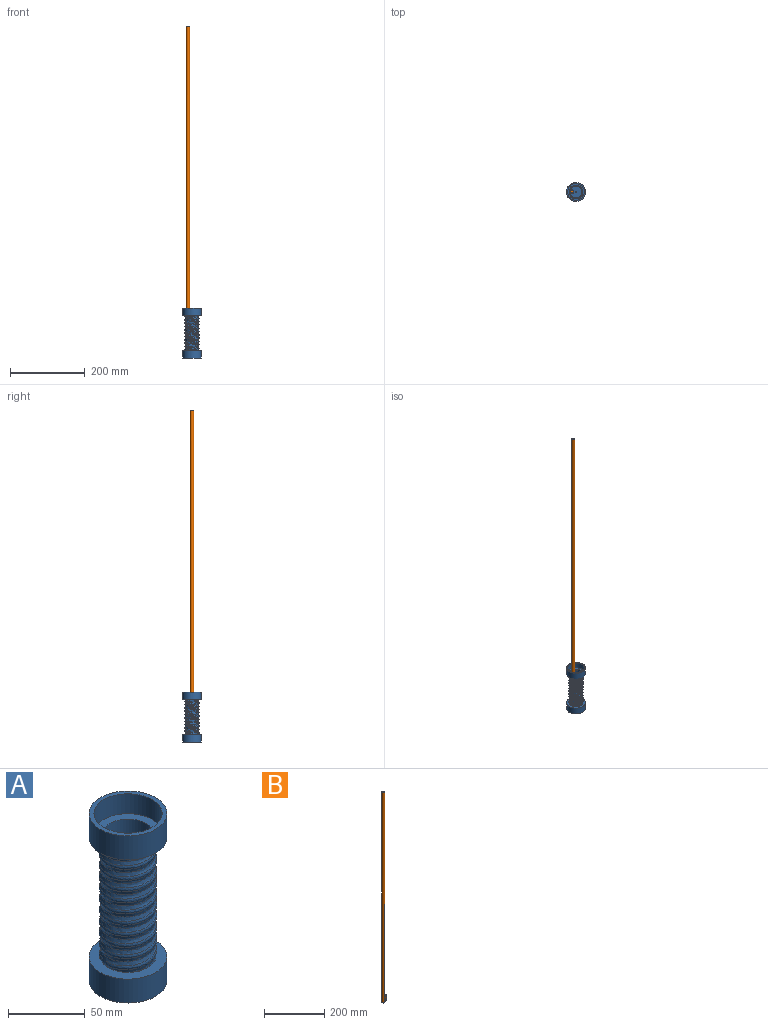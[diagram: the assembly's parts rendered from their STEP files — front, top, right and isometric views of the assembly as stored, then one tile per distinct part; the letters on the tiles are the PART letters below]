
ASSEMBLY  parts=2 mates=1
PART A: 13 faces, bbox 51.3x51.3x133.9 mm
  f0: bspline ~103.35x39.19mm, area 3721.3mm2, adj f1,f2,f5,f8
  f1: bspline ~103.35x39.19mm, area 3734.6mm2, adj f0,f2,f5,f8
  f2: plane 51.31x51.31mm, normal (0,0,1), area 978.2mm2, adj f0,f1,f3,f8
  f3: cylinder r=25.4mm len=50.8mm, axis (0,0,1), area 3040.2mm2, adj f2,f4
  f4: plane 50.8x50.8mm, normal (0,0,-1), area 2026.8mm2, adj f3
  f5: plane 51.31x51.31mm, normal (0,0,-1), area 978.2mm2, adj f0,f1,f6,f8
  f6: cylinder r=25.4mm len=50.8mm, axis (0,0,1), area 3040.2mm2, adj f5,f7
  f7: plane 50.8x50.8mm, normal (0,0,1), area 475mm2, adj f6,f9
  f8: bspline ~101.39x38.6mm, area 3908.7mm2, adj f0,f1,f2,f5
  f9: cylinder r=22.23mm len=44.45mm, axis (0,0,1), area 2216.8mm2, adj f7,f10
  f10: plane 44.45x44.45mm, normal (0,0,1), area 728.1mm2, adj f9,f12
  f11: plane 32.39x32.39mm, normal (0,0,1), area 823.7mm2, adj f12
  f12: cylinder r=16.19mm len=114.3mm, axis (0,0,1), area 11628.9mm2, adj f10,f11
PART B: 7 faces, bbox 16.8x9x854.1 mm
  f0: cylinder r=4.5mm len=854.08mm, axis (0,0,1), area 24107.9mm2, adj f1,f3,f4,f5,f6
  f1: plane 25.4x4.94mm, normal (0,-1,0), area 125.4mm2, adj f0,f2,f4,f5
  f2: cylinder r=1.59mm len=25.4mm, axis (0,0,1), area 211.1mm2, adj f1,f3,f4,f5
  f3: plane 25.4x4.94mm, normal (0,1,0), area 125.4mm2, adj f0,f2,f4,f5
  f4: plane 16.83x9mm, normal (0,0,-1), area 79.1mm2, adj f0,f1,f2,f3
  f5: plane 7.9x3.18mm, normal (0,0,1), area 15.4mm2, adj f0,f1,f2,f3
  f6: plane 9x9mm, normal (0,0,1), area 63.6mm2, adj f0
PLACE A t=(0.6,-0.38,-4.21)mm
PLACE B t=(0.6,-0.38,-10.56)mm
MATE revolute B.f2 <-> A.f12  axis (0,0,1) through (0.6,-0.38,-10.56)mm
